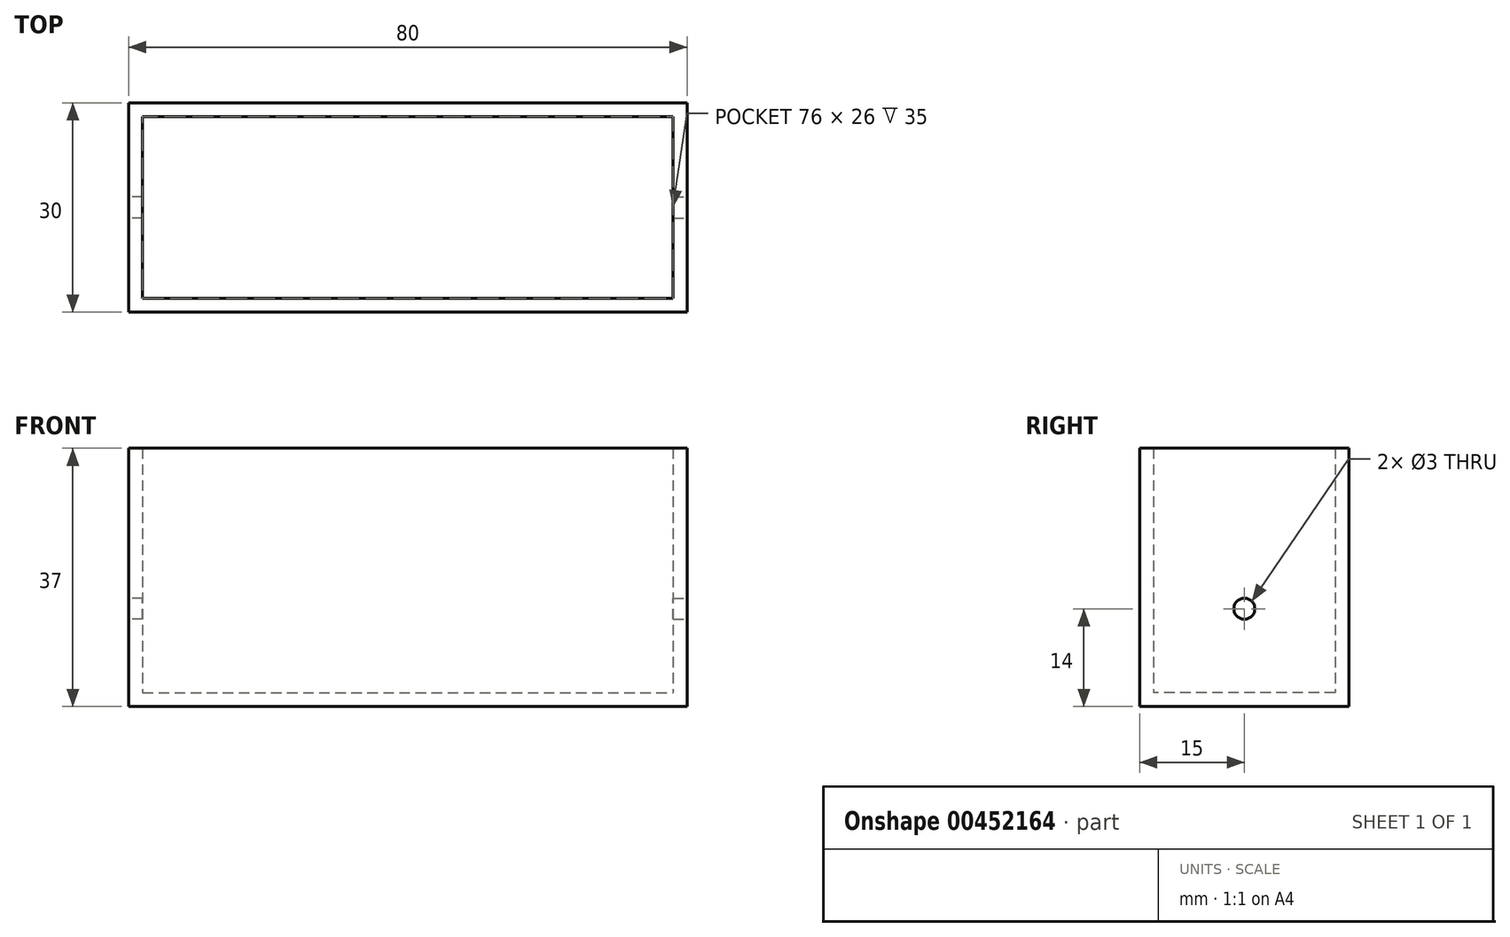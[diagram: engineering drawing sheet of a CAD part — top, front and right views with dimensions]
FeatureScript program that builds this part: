
annotation { "Feature Type Name" : "Feature", "Feature Type Description" : "" }
export const myFeature = defineFeature(function(context is Context, id is Id, definition is map)
    precondition{}
    {
        {
            var Q0;
            Q0=qCreatedBy(makeId("Top.planeOp"),FACE);
            var sketch = newSketch(context, id + "F0", { "sketchPlane" : qUnion([Q0])});
            skLineSegment(sketch, "E0.bottom", {"start": v(-38.42, 15) * mm, "end": v(41.58, 15) * mm});
            skLineSegment(sketch, "E0.top", {"start": v(-38.42, -15) * mm, "end": v(41.58, -15) * mm});
            skLineSegment(sketch, "E0.left", {"start": v(-38.42, 15) * mm, "end": v(-38.42, -15) * mm});
            skLineSegment(sketch, "E0.right", {"start": v(41.58, 15) * mm, "end": v(41.58, -15) * mm});
            skLineSegment(sketch, "E1", {"start": v(-38.42, 0) * mm, "end": v(41.58, 0) * mm, "construction": true});
            skSolve(sketch);
        }
        {
            var Q0;
            Q0 = qSketchRegion(id + "F0", true);
            extrude(context, id + "F1", {"entities" : qUnion([Q0]), "depth" : 37 * mm});
        }
        {
            var Q0;
            Q0=makeQuery(id+"F1.opExtrude","CAP_FACE",FACE,{"disambiguationData":[OSD([sQuery(id+"F0.wireOp",EDGE,"E0.bottom"),sQuery(id+"F0.wireOp",EDGE,"E0.top"),sQuery(id+"F0.wireOp",EDGE,"E0.left"),sQuery(id+"F0.wireOp",EDGE,"E0.right")])],"isStart":false});
            shell(context, id + "F2", {"entities" : qUnion([Q0]), "thickness" : 2 * mm});
        }
        {
            var Q0;
            Q0=qCreatedBy(makeId("Top.planeOp"),FACE);
            var sketch = newSketch(context, id + "F3", { "sketchPlane" : qUnion([Q0])});
            skLineSegment(sketch, "E2.0", {"start": v(-36.42, 13) * mm, "end": v(39.58, 13) * mm});
            skLineSegment(sketch, "E2.1", {"start": v(-36.42, 13) * mm, "end": v(-36.42, -13) * mm});
            skLineSegment(sketch, "E2.2", {"start": v(-36.42, -13) * mm, "end": v(39.58, -13) * mm});
            skLineSegment(sketch, "E2.3", {"start": v(39.58, 13) * mm, "end": v(39.58, -13) * mm});
            skSolve(sketch);
        }
        {
            var Q0;
            Q0=makeQuery(id+"F1.opExtrude","SWEPT_FACE",FACE,{"disambiguationData":[OSD([sQuery(id+"F0.wireOp",EDGE,"E0.right")])]});
            var sketch = newSketch(context, id + "F4", { "sketchPlane" : qUnion([Q0])});
            skLineSegment(sketch, "E3", {"start": v(0, 37) * mm, "end": v(0, 0) * mm, "construction": true});
            skCircle(sketch, "E4", {"center": v(0, 14) * mm, "radius": 1.5 * mm});
            skEllipse(sketch, "E5", {"center": v(0, 14.72) * mm, "majorRadius": 5 * mm, "minorRadius": 3.5 * mm, "majorAxis": v(0, -1), "construction": true});
            skSolve(sketch);
        }
        {
            var Q0;
            Q0=makeQuery(id+"F4.imprint","IMPRINT",FACE,{"disambiguationData":[TD([[makeQuery(id+"F4.imprint","IMPRINT",EDGE,{"derivedFrom":sQuery(id+"F4.wireOp",EDGE,"E4")}),1.0]])]});
            var Q1;
            Q1=sQuery(id+"F4.wireOp",EDGE,"E4");
            extrude(context, id + "F5", {"entities" : qUnion([Q0]), "operationType" : NewBodyOperationType.REMOVE, "surfaceEntities" : qUnion([Q1]), "oppositeDirection" : true, "depth" : 25 * mm});
        }
        {
            var Q0;
            Q0=makeQuery(id+"F1.opExtrude","SWEPT_FACE",FACE,{"disambiguationData":[OSD([sQuery(id+"F0.wireOp",EDGE,"E0.left")])]});
            var sketch = newSketch(context, id + "F6", { "sketchPlane" : qUnion([Q0])});
            skCircle(sketch, "E6", {"center": v(0, 14) * mm, "radius": 1.5 * mm});
            skSolve(sketch);
        }
        {
            var Q0;
            Q0 = qSketchRegion(id + "F6", true);
            extrude(context, id + "F7", {"entities" : qUnion([Q0]), "operationType" : NewBodyOperationType.REMOVE, "oppositeDirection" : true, "depth" : 3 * mm});
        }
    });
